# Revit family: KEUCO_34954010100
name_source: partatom
category: Sonderausstattung
revit_build: Autodesk Revit 2016 (Build: 20150220_1215(x64)
units: mm (PartAtom-declared; Revit-internal decimal feet)

## family parameters
Arbeitsebenenbasiert = Nein
Beim Laden mit Abzugskörper schneiden = Nein
Bemaßung runder Anschluss = Durchmesser verwenden
Gemeinsam genutzt = Nein
Immer vertikal = Ja
Raumberechnungspunkt = Nein
Teiletyp = Normal

## types (2) — shared parameters
Beschreibung = Spendergehäuse für 0,5 l Euronormflasche
mit integrierter Pumpe (baugleich z.B. Bode
Euronormflasche 0,5 l Sterilium), mit abnehmbarer
Tropfschale aus Kunststoff
Gewicht = 320.7
Hersteller = KEUCO
Kategorie = ACC
Preisgruppe = 1
Serie = Plan
URL = https://www.keuco.com
Verwendung = CA / GWC / WP

## per-type parameters (varying)
| type | Ausschreibungstext |
| 34954010100 | KEUCO Flüssigseifen- und Desinfektionsmittelspender 34954010100
KEUCO PLAN Flüssigseifen- und Desinfektionsmittelspender, verchromt,
in ästhetischem, funktionalem Design,
mit abnehmbarer Tropfschale aus Kunststoff (anthrazit),
für 0,5 L Euronormflaschen, 
Die Euronormflaschen und Pumpen sind nicht im Lieferumfang enthalten:

Folgende Euronormflaschen können eingesetzt werden:
Bode (Art-Nr 106650/ PZN 00970709; Dosierpumpe Art-Nr 9804241), 
B. Braun Petzold GmbH (Art-Nr 19159/ PZN 01980561; Dosierpumpe Art-Nr 3908380 ), 
Ecolab GmbH & Co. OHG (Art-Nr 3017360/ PZN 07356119; Dosierpumpe Art-Nr 10000015) oder
Dr. Schumacher Hygiene & Desinfektion (Art-Nr 00-409-005; Dosierpumpe Art-Nr 00-906-005-02)

hochglanzverchromtes Gehäuse mit transparentem Sichtfenster 
zur Identifikation von: Art der Flüssigkeit, Ablaufdatum und Füllstandsanzeige, 
einfaches Wechseln und Reinigen der Euronormflaschen durch frontale Entnahme, 
Gesamtausladung inkl. Tropfschale 250 mm (ohne Tropfschale 170 mm), 
Bauhöhe 302 mm, Breite 110 mm
Der Spender wird verdeckt angebracht.
Lieferung inkl. korrosionsfreiem Befestigungsmaterial |
| 34954170100 | KEUCO Flüssigseifen- und Desinfektionsmittelspender 34954010100
KEUCO PLAN Flüssigseifen- und Desinfektionsmittelspender, verchromt,
in ästhetischem, funktionalem Design,
mit abnehmbarer Tropfschale aus Kunststoff (anthrazit),
für 0,5 L Euronormflaschen, 
Die Euronormflaschen und Pumpen sind nicht im Lieferumfang enthalten:

Folgende Euronormflaschen können eingesetzt werden:
Bode (Art-Nr 106650/ PZN 00970709; Dosierpumpe Art-Nr 9804241), 
B. Braun Petzold GmbH (Art-Nr 19159/ PZN 01980561; Dosierpumpe Art-Nr 3908380 ), 
Ecolab GmbH & Co. OHG (Art-Nr 3017360/ PZN 07356119; Dosierpumpe Art-Nr 10000015) oder
Dr. Schumacher Hygiene & Desinfektion (Art-Nr 00-409-005; Dosierpumpe Art-Nr 00-906-005-02)

hochglanzverchromtes Gehäuse mit transparentem Sichtfenster 
zur Identifikation von: Art der Flüssigkeit, Ablaufdatum und Füllstandsanzeige, 
einfaches Wechseln und Reinigen der Euronormflaschen durch frontale Entnahme, 
Gesamtausladung inkl. Tropfschale 250 mm (ohne Tropfschale 170 mm), 
Bauhöhe 302 mm, Breite 110 mm
Der Spender wird verdeckt angebracht.
Lieferung inkl. korrosionsfreiem Befestigungsmaterial. |

note: column(s) folded — value = type name in every type: Artikelnummer

## geometry (parser evidence)
native form markers: Blend x2, Sweep x3
no freeform markers — native parametric forms only
